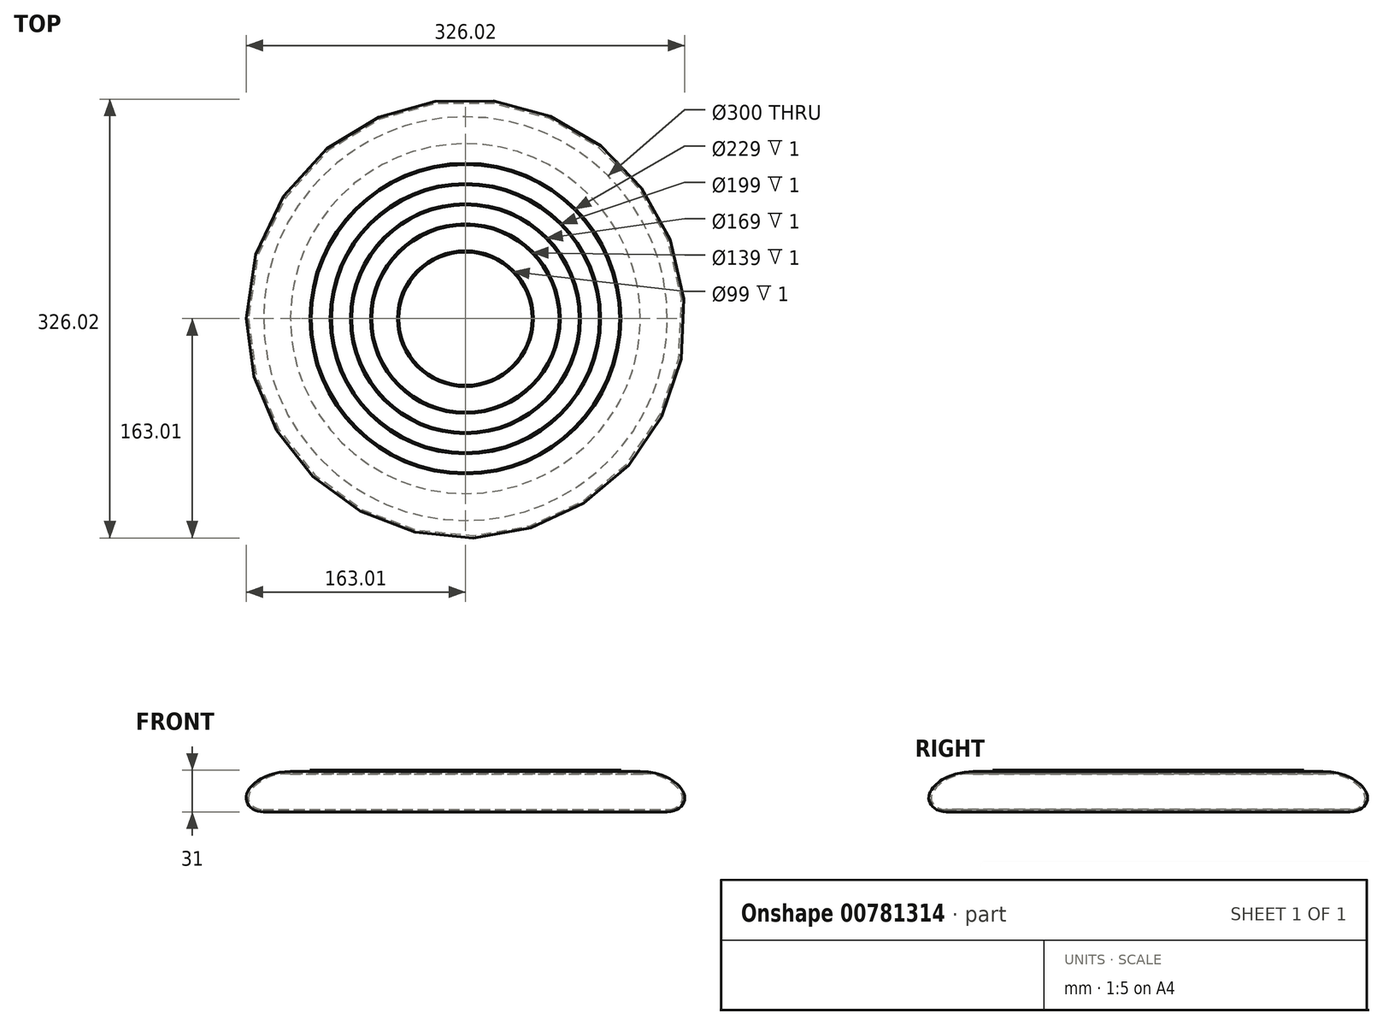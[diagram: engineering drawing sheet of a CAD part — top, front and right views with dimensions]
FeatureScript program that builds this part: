
annotation { "Feature Type Name" : "Feature", "Feature Type Description" : "" }
export const myFeature = defineFeature(function(context is Context, id is Id, definition is map)
    precondition{}
    {
        {
            var Q0;
            Q0=qCreatedBy(makeId("Front.planeOp"),FACE);
            var sketch = newSketch(context, id + "F0", { "sketchPlane" : qUnion([Q0])});
            skLineSegment(sketch, "E0", {"start": v(0, 0) * mm, "end": v(0, 30) * mm, "construction": true});
            skLineSegment(sketch, "E1", {"start": v(0, 0) * mm, "end": v(150, 0) * mm, "construction": true});
            skFitSpline(sketch, "E2", {"points": [v(130, 30) * mm, v(163, 10) * mm, v(150, 0) * mm], "startDerivative": vector(99.12, 0) * mm, "endDerivative": vector(-50.48, 0) * mm});
            skLineSegment(sketch, "E3.1", {"start": v(0, 28.25) * mm, "end": v(130, 28.25) * mm});
            skLineSegment(sketch, "E4", {"start": v(150, 1.75) * mm, "end": v(150, 0) * mm});
            skFitSpline(sketch, "E5.0", {"points": [v(130, 28.25) * mm, v(134, 28.25) * mm, v(141.41, 27.3) * mm, v(148.97, 24.41) * mm, v(153.8, 21.44) * mm, v(156.76, 19) * mm, v(159.02, 16.45) * mm, v(160.27, 14.33) * mm, v(160.9, 12.72) * mm, v(161.18, 11.56) * mm, v(161.29, 10.46) * mm, v(161.22, 9.43) * mm, v(160.98, 8.43) * mm, v(160.46, 7.14) * mm, v(159.41, 5.6) * mm, v(157.6, 4.01) * mm, v(155.35, 2.76) * mm, v(152.77, 1.95) * mm, v(150.93, 1.75) * mm, v(150, 1.75) * mm]});
            skLineSegment(sketch, "E6", {"start": v(0, 30) * mm, "end": v(0, 28.25) * mm});
            skLineSegment(sketch, "E7", {"start": v(0, 30) * mm, "end": v(49.5, 30) * mm});
            skLineSegment(sketch, "E8", {"start": v(49.5, 30) * mm, "end": v(49.5, 31) * mm});
            skLineSegment(sketch, "E9", {"start": v(49.5, 31) * mm, "end": v(50.5, 31) * mm});
            skLineSegment(sketch, "E10", {"start": v(50.5, 31) * mm, "end": v(50.5, 30) * mm});
            skLineSegment(sketch, "E11", {"start": v(50.5, 30) * mm, "end": v(69.5, 30) * mm});
            skLineSegment(sketch, "E12", {"start": v(69.5, 30) * mm, "end": v(69.5, 31) * mm});
            skLineSegment(sketch, "E13", {"start": v(69.5, 31) * mm, "end": v(70.5, 31) * mm});
            skLineSegment(sketch, "E14", {"start": v(70.5, 31) * mm, "end": v(70.5, 30) * mm});
            skLineSegment(sketch, "E15", {"start": v(70.5, 30) * mm, "end": v(84.5, 30) * mm});
            skLineSegment(sketch, "E16", {"start": v(84.5, 30) * mm, "end": v(84.5, 31) * mm});
            skLineSegment(sketch, "E17", {"start": v(84.5, 31) * mm, "end": v(85.5, 31) * mm});
            skLineSegment(sketch, "E18", {"start": v(85.5, 31) * mm, "end": v(85.5, 30) * mm});
            skLineSegment(sketch, "E19", {"start": v(85.5, 30) * mm, "end": v(99.5, 30) * mm});
            skLineSegment(sketch, "E20", {"start": v(99.5, 30) * mm, "end": v(99.5, 31) * mm});
            skLineSegment(sketch, "E21", {"start": v(99.5, 31) * mm, "end": v(100.5, 31) * mm});
            skLineSegment(sketch, "E22", {"start": v(100.5, 31) * mm, "end": v(100.5, 30) * mm});
            skLineSegment(sketch, "E23", {"start": v(100.5, 30) * mm, "end": v(114.5, 30) * mm});
            skLineSegment(sketch, "E24", {"start": v(114.5, 30) * mm, "end": v(114.5, 31) * mm});
            skLineSegment(sketch, "E25", {"start": v(114.5, 31) * mm, "end": v(115.5, 31) * mm});
            skLineSegment(sketch, "E26", {"start": v(115.5, 31) * mm, "end": v(115.5, 30) * mm});
            skLineSegment(sketch, "E27", {"start": v(115.5, 30) * mm, "end": v(130, 30) * mm});
            skLineSegment(sketch, "E28", {"start": v(50, 31) * mm, "end": v(50, 28.25) * mm, "construction": true});
            skLineSegment(sketch, "E29", {"start": v(70, 31) * mm, "end": v(70, 28.25) * mm, "construction": true});
            skLineSegment(sketch, "E30", {"start": v(85, 31) * mm, "end": v(85, 28.25) * mm, "construction": true});
            skLineSegment(sketch, "E31", {"start": v(100, 31) * mm, "end": v(100, 28.25) * mm, "construction": true});
            skLineSegment(sketch, "E32", {"start": v(115, 31) * mm, "end": v(115, 28.25) * mm, "construction": true});
            skSolve(sketch);
        }
        {
            var Q0;
            Q0=makeQuery(id+"F0.imprint","IMPRINT",FACE,{"disambiguationData":[TD([[makeQuery(id+"F0.imprint","IMPRINT",EDGE,{"derivedFrom":sQuery(id+"F0.wireOp",EDGE,"E2")}),-1.0]])]});
            var Q1;
            Q1=sQuery(id+"F0.wireOp",EDGE,"E0");
            revolve(context, id + "F1", {"surfaceOperationType" : NewSurfaceOperationType.NEW, "entities" : qUnion([Q0]), "axis" : qUnion([Q1]), "revolveType" : RevolveType.FULL});
        }
    });
